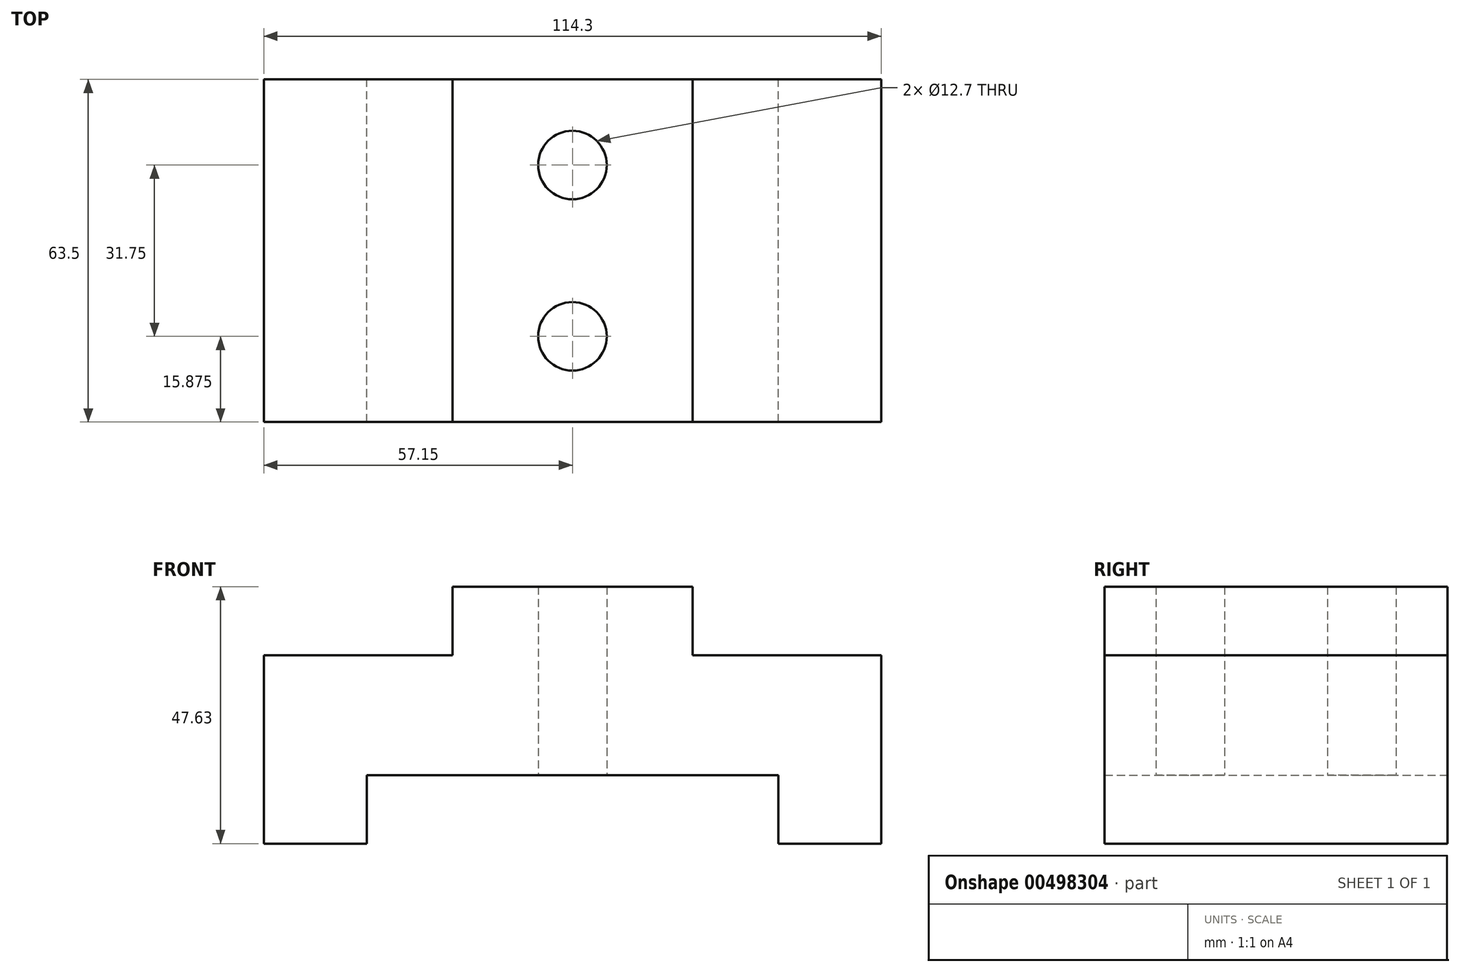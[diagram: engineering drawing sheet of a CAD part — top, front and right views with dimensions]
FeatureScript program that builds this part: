
annotation { "Feature Type Name" : "Feature", "Feature Type Description" : "" }
export const myFeature = defineFeature(function(context is Context, id is Id, definition is map)
    precondition{}
    {
        {
            var Q0;
            Q0=qCreatedBy(makeId("Front.planeOp"),FACE);
            var sketch = newSketch(context, id + "F0", { "sketchPlane" : qUnion([Q0])});
            skLineSegment(sketch, "E0", {"start": v(-38.1, 0) * mm, "end": v(38.1, 0) * mm});
            skLineSegment(sketch, "E1", {"start": v(38.1, 0) * mm, "end": v(38.1, -12.7) * mm});
            skLineSegment(sketch, "E2", {"start": v(38.1, -12.7) * mm, "end": v(57.15, -12.7) * mm});
            skLineSegment(sketch, "E3", {"start": v(57.15, -12.7) * mm, "end": v(57.15, 22.23) * mm});
            skLineSegment(sketch, "E4", {"start": v(57.15, 22.23) * mm, "end": v(22.23, 22.23) * mm});
            skLineSegment(sketch, "E5", {"start": v(22.23, 22.23) * mm, "end": v(22.23, 34.93) * mm});
            skLineSegment(sketch, "E6", {"start": v(22.23, 34.93) * mm, "end": v(-22.23, 34.93) * mm});
            skLineSegment(sketch, "E7", {"start": v(-22.23, 34.93) * mm, "end": v(-22.23, 22.23) * mm});
            skLineSegment(sketch, "E8", {"start": v(-22.23, 22.23) * mm, "end": v(-57.15, 22.23) * mm});
            skLineSegment(sketch, "E9", {"start": v(-57.15, 22.23) * mm, "end": v(-57.15, -12.7) * mm});
            skLineSegment(sketch, "E10", {"start": v(-57.15, -12.7) * mm, "end": v(-38.1, -12.7) * mm});
            skLineSegment(sketch, "E11", {"start": v(-38.1, 0) * mm, "end": v(-38.1, -12.7) * mm});
            skPoint(sketch, "E12", {"position": v(0, 0) * mm});
            skSolve(sketch);
        }
        {
            var Q0;
            Q0=makeQuery(id+"F0.imprint","IMPRINT",FACE,{"disambiguationData":[TD([[makeQuery(id+"F0.imprint","IMPRINT",EDGE,{"derivedFrom":sQuery(id+"F0.wireOp",EDGE,"E0")}),1.0]])]});
            extrude(context, id + "F1", {"entities" : qUnion([Q0]), "depth" : 63.5 * mm});
        }
        {
            var Q0;
            Q0=qCreatedBy(makeId("Top.planeOp"),FACE);
            var sketch = newSketch(context, id + "F2", { "sketchPlane" : qUnion([Q0])});
            skCircle(sketch, "E13", {"center": v(0, -15.88) * mm, "radius": 6.35 * mm});
            skCircle(sketch, "E14", {"center": v(0, -47.63) * mm, "radius": 6.35 * mm});
            skSolve(sketch);
        }
        {
            var Q0;
            Q0=sQuery(id+"F2.wireOp",VERTEX,"E14.center");
            var Q1;
            Q1=makeQuery(id+"F1.opExtrude","SWEPT_BODY",BODY,{"disambiguationData":[OSD([sQuery(id+"F0.wireOp",EDGE,"E0"),sQuery(id+"F0.wireOp",EDGE,"E1"),sQuery(id+"F0.wireOp",EDGE,"E2"),sQuery(id+"F0.wireOp",EDGE,"E3"),sQuery(id+"F0.wireOp",EDGE,"E4"),sQuery(id+"F0.wireOp",EDGE,"E5"),sQuery(id+"F0.wireOp",EDGE,"E6"),sQuery(id+"F0.wireOp",EDGE,"E7"),sQuery(id+"F0.wireOp",EDGE,"E8"),sQuery(id+"F0.wireOp",EDGE,"E9"),sQuery(id+"F0.wireOp",EDGE,"E10"),sQuery(id+"F0.wireOp",EDGE,"E11")])]});
            hole(context, id + "F3", {"style" : HoleStyle.SIMPLE, "endStyle" : HoleEndStyle.THROUGH, "oppositeDirection" : true, "holeDiameter" : 12.7 * mm, "isTappedThrough" : true, "tappedDepth" : 12.7 * mm, "tapClearance" : 3, "locations" : qUnion([Q0]), "scope" : qUnion([Q1])});
        }
        {
            var Q0;
            Q0=sQuery(id+"F2.wireOp",VERTEX,"E13.center");
            var Q1;
            Q1=makeQuery(id+"F1.opExtrude","SWEPT_BODY",BODY,{"disambiguationData":[OSD([sQuery(id+"F0.wireOp",EDGE,"E0"),sQuery(id+"F0.wireOp",EDGE,"E1"),sQuery(id+"F0.wireOp",EDGE,"E2"),sQuery(id+"F0.wireOp",EDGE,"E3"),sQuery(id+"F0.wireOp",EDGE,"E4"),sQuery(id+"F0.wireOp",EDGE,"E5"),sQuery(id+"F0.wireOp",EDGE,"E6"),sQuery(id+"F0.wireOp",EDGE,"E7"),sQuery(id+"F0.wireOp",EDGE,"E8"),sQuery(id+"F0.wireOp",EDGE,"E9"),sQuery(id+"F0.wireOp",EDGE,"E10"),sQuery(id+"F0.wireOp",EDGE,"E11")])]});
            hole(context, id + "F4", {"style" : HoleStyle.SIMPLE, "endStyle" : HoleEndStyle.THROUGH, "oppositeDirection" : true, "holeDiameter" : 12.7 * mm, "isTappedThrough" : true, "tappedDepth" : 12.7 * mm, "tapClearance" : 3, "locations" : qUnion([Q0]), "scope" : qUnion([Q1])});
        }
    });
